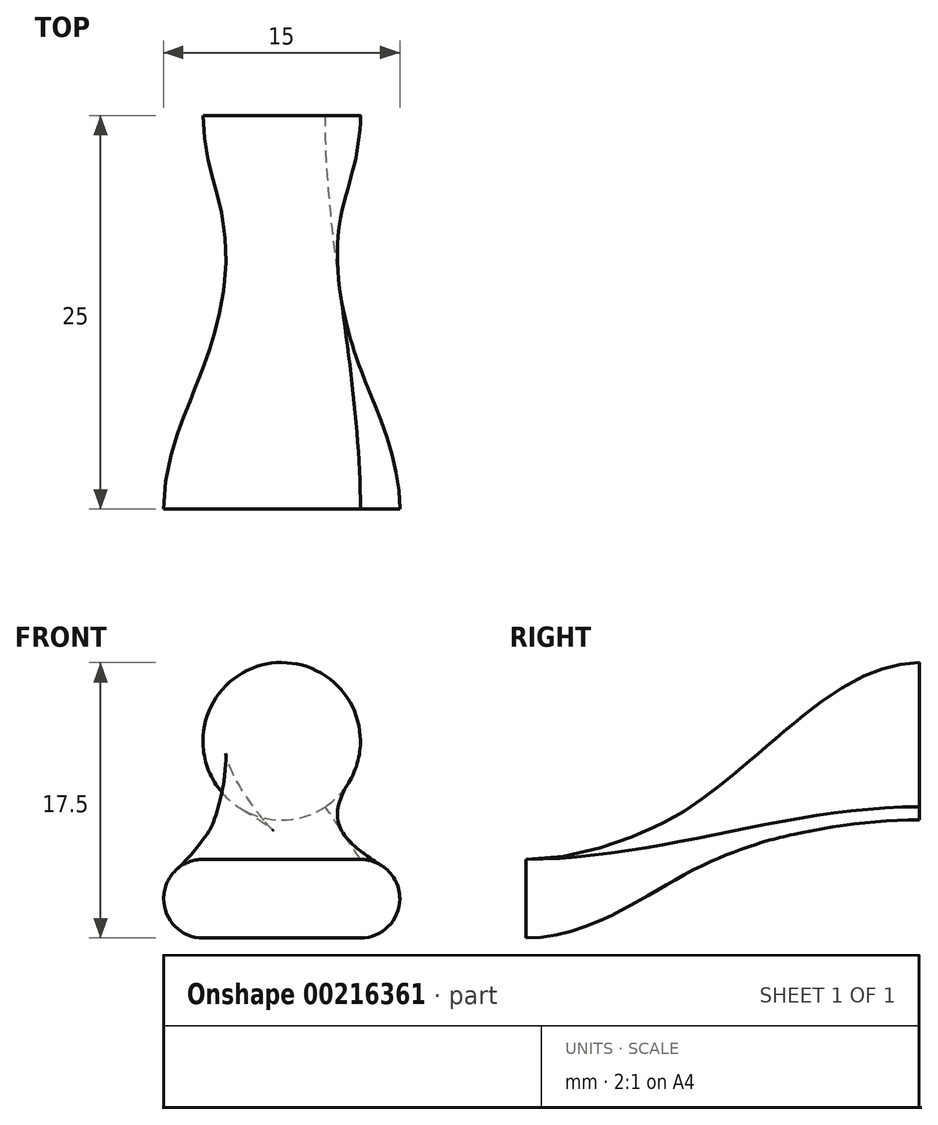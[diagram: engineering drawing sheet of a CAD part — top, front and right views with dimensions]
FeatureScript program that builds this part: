
annotation { "Feature Type Name" : "Feature", "Feature Type Description" : "" }
export const myFeature = defineFeature(function(context is Context, id is Id, definition is map)
    precondition{}
    {
        {
            var Q0;
            Q0=qCreatedBy(makeId("Front.planeOp"),FACE);
            cPlane(context, id + "F0", {"entities" : qUnion([Q0]), "cplaneType" : CPlaneType.OFFSET, "offset" : 25 * mm, "oppositeDirection" : true, "width" : 150 * mm, "height" : 150 * mm});
        }
        {
            var Q0;
            Q0=qCreatedBy(makeId("Front.planeOp"),FACE);
            var sketch = newSketch(context, id + "F1", { "sketchPlane" : qUnion([Q0])});
            skLineSegment(sketch, "E0.bottom", {"start": v(5, 2.5) * mm, "end": v(-5, 2.5) * mm});
            skLineSegment(sketch, "E0.top", {"start": v(5, -2.5) * mm, "end": v(-5, -2.5) * mm});
            skLineSegment(sketch, "E0.left", {"start": v(7.5, 0) * mm, "end": v(7.5, 0) * mm});
            skLineSegment(sketch, "E0.right", {"start": v(-7.5, 0) * mm, "end": v(-7.5, 0) * mm});
            skPoint(sketch, "E0.middle", {"position": v(0, 0) * mm});
            skPoint(sketch, "E1.visualSharp", {"position": v(7.5, 2.5) * mm});
            skArc(sketch, "E1.filletArc", {"start": v(7.5, 0) * mm, "mid": v(6.77, 1.77) * mm, "end": v(5, 2.5) * mm});
            skPoint(sketch, "E2.visualSharp", {"position": v(-7.5, 2.5) * mm});
            skArc(sketch, "E2.filletArc", {"start": v(-5, 2.5) * mm, "mid": v(-6.77, 1.77) * mm, "end": v(-7.5, 0) * mm});
            skPoint(sketch, "E3.visualSharp", {"position": v(-7.5, -2.5) * mm});
            skArc(sketch, "E3.filletArc", {"start": v(-7.5, 0) * mm, "mid": v(-6.77, -1.77) * mm, "end": v(-5, -2.5) * mm});
            skPoint(sketch, "E4.visualSharp", {"position": v(7.5, -2.5) * mm});
            skArc(sketch, "E4.filletArc", {"start": v(5, -2.5) * mm, "mid": v(6.77, -1.77) * mm, "end": v(7.5, 0) * mm});
            skSolve(sketch);
        }
        {
            var Q0;
            Q0=qCreatedBy(id+"F0.planeOp",FACE);
            var sketch = newSketch(context, id + "F2", { "sketchPlane" : qUnion([Q0])});
            skCircle(sketch, "E5", {"center": v(0, 10) * mm, "radius": 5 * mm});
            skSolve(sketch);
        }
        {
            var Q0;
            Q0=makeQuery(id+"F1.imprint","IMPRINT",FACE,{"disambiguationData":[TD([[makeQuery(id+"F1.imprint","IMPRINT",EDGE,{"derivedFrom":sQuery(id+"F1.wireOp",EDGE,"E0.bottom")}),1.0]])]});
            var Q1;
            Q1 = qSketchRegion(id + "F2", true);
            loft(context, id + "F3", {"startCondition" : LoftEndDerivativeType.NORMAL_TO_PROFILE, "startMagnitude" : 1, "endCondition" : LoftEndDerivativeType.NORMAL_TO_PROFILE, "endMagnitude" : 1, "sheetProfilesArray" : [{ "sheetProfileEntities" : qUnion([Q0]) }, { "sheetProfileEntities" : qUnion([Q1]) }]});
        }
    });
